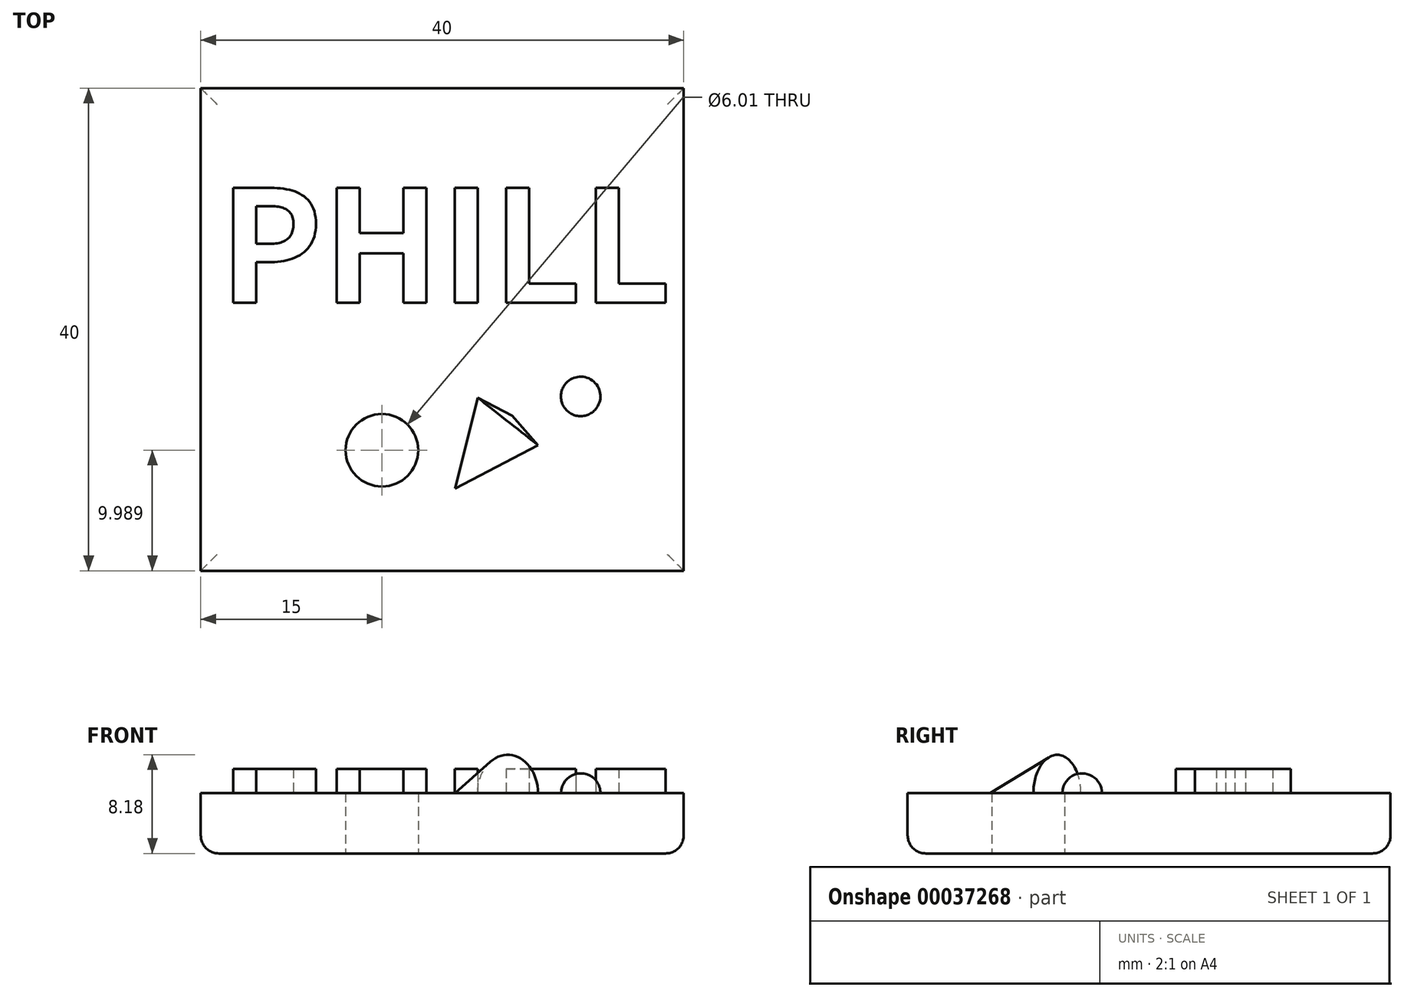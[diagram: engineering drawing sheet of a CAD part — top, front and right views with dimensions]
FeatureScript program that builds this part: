
annotation { "Feature Type Name" : "Feature", "Feature Type Description" : "" }
export const myFeature = defineFeature(function(context is Context, id is Id, definition is map)
    precondition{}
    {
        {
            var Q0;
            Q0=qCreatedBy(makeId("Top.planeOp"),FACE);
            var sketch = newSketch(context, id + "F0", { "sketchPlane" : qUnion([Q0])});
            skLineSegment(sketch, "E0", {"start": v(0, 20) * mm, "end": v(0, -20) * mm, "construction": true});
            skLineSegment(sketch, "E1.0", {"start": v(-20, 20) * mm, "end": v(-20, -20) * mm, "construction": true});
            skLineSegment(sketch, "E2", {"start": v(-20, 0) * mm, "end": v(20, 0) * mm, "construction": true});
            skLineSegment(sketch, "E3.0", {"start": v(-20, -20) * mm, "end": v(20, -20) * mm, "construction": true});
            skLineSegment(sketch, "E4.0", {"start": v(-5, 20) * mm, "end": v(-5, -20) * mm, "construction": true});
            skLineSegment(sketch, "E5.0", {"start": v(20, 20) * mm, "end": v(20, -20) * mm, "construction": true});
            skLineSegment(sketch, "E6.0", {"start": v(-20, 20) * mm, "end": v(20, 20) * mm, "construction": true});
            skPoint(sketch, "E7.orphan", {"position": v(0, 46.15) * mm});
            skPoint(sketch, "E8.orphan", {"position": v(-29, 0) * mm});
            skLineSegment(sketch, "E9", {"start": v(-20, 20) * mm, "end": v(20, 20) * mm});
            skLineSegment(sketch, "E10", {"start": v(20, -20) * mm, "end": v(20, 20) * mm});
            skLineSegment(sketch, "E11", {"start": v(-20, -20) * mm, "end": v(20, -20) * mm});
            skLineSegment(sketch, "E12", {"start": v(-20, 20) * mm, "end": v(-20, -20) * mm});
            skCircle(sketch, "E13", {"center": v(-5, -10.01) * mm, "radius": 3 * mm});
            skSolve(sketch);
        }
        {
            var Q0;
            Q0=makeQuery(id+"F0.imprint","IMPRINT",FACE,{"disambiguationData":[TD([[makeQuery(id+"F0.imprint","IMPRINT",EDGE,{"derivedFrom":sQuery(id+"F0.wireOp",EDGE,"E9")}),-1.0]])]});
            extrude(context, id + "F1", {"entities" : qUnion([Q0]), "depth" : 5 * mm});
        }
        {
            var Q0;
            Q0=makeQuery(id+"F1.opExtrude","CAP_EDGE",EDGE,{"disambiguationData":[OSD([sQuery(id+"F0.wireOp",EDGE,"E12")])],"isStart":true});
            var Q1;
            Q1=makeQuery(id+"F1.opExtrude","CAP_EDGE",EDGE,{"disambiguationData":[OSD([sQuery(id+"F0.wireOp",EDGE,"E9")])],"isStart":true});
            var Q2;
            Q2=makeQuery(id+"F1.opExtrude","CAP_EDGE",EDGE,{"disambiguationData":[OSD([sQuery(id+"F0.wireOp",EDGE,"E11")])],"isStart":true});
            var Q3;
            Q3=makeQuery(id+"F1.opExtrude","CAP_EDGE",EDGE,{"disambiguationData":[OSD([sQuery(id+"F0.wireOp",EDGE,"E10")])],"isStart":true});
            fillet(context, id + "F2", {"entities" : qUnion([Q0, Q1, Q2, Q3]), "radius" : 1.5 * mm, "tangentPropagation" : true, "allowEdgeOverflow" : false});
        }
        {
            var Q0;
            Q0=makeQuery(id+"F1.opExtrude","CAP_FACE",FACE,{"disambiguationData":[OSD([sQuery(id+"F0.wireOp",EDGE,"E9"),sQuery(id+"F0.wireOp",EDGE,"E10"),sQuery(id+"F0.wireOp",EDGE,"E11"),sQuery(id+"F0.wireOp",EDGE,"E12")])],"isStart":false});
            var sketch = newSketch(context, id + "F3", { "sketchPlane" : qUnion([Q0])});
            skLineSegment(sketch, "E14.0.0", {"start": v(-18.5, 18.5) * mm, "end": v(-18.5, -18.5) * mm});
            skLineSegment(sketch, "E14.0.1", {"start": v(-18.5, -18.5) * mm, "end": v(18.5, -18.5) * mm});
            skLineSegment(sketch, "E14.0.2", {"start": v(18.5, -18.5) * mm, "end": v(18.5, 18.5) * mm});
            skLineSegment(sketch, "E14.0.3", {"start": v(18.5, 18.5) * mm, "end": v(-18.5, 18.5) * mm});
            skText(sketch, "E15", { "text": "PHILL", "fontName": "NotoSansCJKsc-Bold.otf"});
            skCircle(sketch, "E16", {"center": v(9.55, -9.57) * mm, "radius": 4.46 * mm});
            skLineSegment(sketch, "E17", {"start": v(12.79, -6.5) * mm, "end": v(9.55, -9.57) * mm});
            skLineSegment(sketch, "E18", {"start": v(9.55, -9.57) * mm, "end": v(6.3, -12.63) * mm});
            skCircle(sketch, "E19", {"center": v(11.47, -5.54) * mm, "radius": 1.63 * mm});
            skLineSegment(sketch, "E20", {"start": v(5.8, -7.15) * mm, "end": v(1.07, -13.17) * mm});
            skLineSegment(sketch, "E21", {"start": v(1.07, -13.17) * mm, "end": v(2.93, -5.66) * mm});
            skLineSegment(sketch, "E22", {"start": v(2.93, -5.66) * mm, "end": v(5.8, -7.15) * mm});
            skLineSegment(sketch, "E23", {"start": v(12.79, -6.5) * mm, "end": v(6.3, -12.63) * mm});
            skLineSegment(sketch, "E24", {"start": v(12.79, -6.5) * mm, "end": v(10.14, -4.6) * mm});
            const initialGuessF3  = {"E15": [-0.0185, 0.0022, 1, 0, 0.00928]};
            skSetInitialGuess(sketch, initialGuessF3);
            skSolve(sketch);
        }
        {
            var Q0;
            Q0=makeQuery(id+"F3.imprint","IMPRINT",FACE,{"disambiguationData":[TD([[makeQuery(id+"F3.imprint","IMPRINT",EDGE,{"derivedFrom":sQuery(id+"F3.wireOp",EDGE,"E15.sketch_text.stroke-0")}),1.0]])]});
            var Q1;
            Q1=makeQuery(id+"F3.imprint","IMPRINT",FACE,{"disambiguationData":[TD([[makeQuery(id+"F3.imprint","IMPRINT",EDGE,{"derivedFrom":sQuery(id+"F3.wireOp",EDGE,"E15.sketch_text.stroke-12")}),1.0]])]});
            var Q2;
            Q2=makeQuery(id+"F3.imprint","IMPRINT",FACE,{"disambiguationData":[TD([[makeQuery(id+"F3.imprint","IMPRINT",EDGE,{"derivedFrom":sQuery(id+"F3.wireOp",EDGE,"E15.sketch_text.stroke-24")}),1.0]])]});
            var Q3;
            Q3=makeQuery(id+"F3.imprint","IMPRINT",FACE,{"disambiguationData":[TD([[makeQuery(id+"F3.imprint","IMPRINT",EDGE,{"derivedFrom":sQuery(id+"F3.wireOp",EDGE,"E15.sketch_text.stroke-28")}),1.0]])]});
            var Q4;
            Q4=makeQuery(id+"F3.imprint","IMPRINT",FACE,{"disambiguationData":[TD([[makeQuery(id+"F3.imprint","IMPRINT",EDGE,{"derivedFrom":sQuery(id+"F3.wireOp",EDGE,"E15.sketch_text.stroke-34")}),1.0]])]});
            extrude(context, id + "F4", {"entities" : qUnion([Q0, Q1, Q2, Q3, Q4]), "operationType" : NewBodyOperationType.ADD, "depth" : 2 * mm});
        }
        {
            var Q0;
            Q0=makeQuery(id+"F3.imprint","IMPRINT",FACE,{"disambiguationData":[TD([[makeQuery(id+"F3.imprint","IMPRINT",EDGE,{"derivedFrom":sQuery(id+"F3.wireOp",EDGE,"E20")}),-1.0]])]});
            var Q1;
            Q1=sQuery(id+"F3.wireOp",EDGE,"E20");
            revolve(context, id + "F5", {"operationType" : NewBodyOperationType.ADD, "entities" : qUnion([Q0]), "axis" : qUnion([Q1]), "revolveType" : RevolveType.FULL});
        }
        {
            var Q0;
            {var subQ0=sQuery(id+"F3.wireOp",EDGE,"E24");var subQ1=sQuery(id+"F3.wireOp",EDGE,"E19");var subQ5=makeQuery(id+"F3.imprint","INTERSECT",VERTEX,{"derivedFrom":[subQ1,subQ0]});Q0=makeQuery(id+"F3.imprint","IMPRINT",FACE,{"disambiguationData":[TD([[makeQuery(id+"F3.imprint","IMPRINT",EDGE,{"disambiguationData":[TD([[subQ5,1.0]])],"derivedFrom":subQ0}),-1.0]])]});}
            var Q1;
            {var subQ0=sQuery(id+"F3.wireOp",EDGE,"E24");var subQ1=sQuery(id+"F3.wireOp",EDGE,"E16");var subQ3=makeQuery(id+"F3.imprint","INTERSECT",VERTEX,{"derivedFrom":[subQ1,subQ0]});Q1=makeQuery(id+"F3.imprint","IMPRINT",FACE,{"disambiguationData":[TD([[makeQuery(id+"F3.imprint","IMPRINT",EDGE,{"disambiguationData":[TD([[subQ3,1.0]])],"derivedFrom":subQ1}),1.0]])]});}
            var Q2;
            Q2=sQuery(id+"F3.wireOp",EDGE,"E24");
            revolve(context, id + "F6", {"operationType" : NewBodyOperationType.ADD, "entities" : qUnion([Q0, Q1]), "axis" : qUnion([Q2]), "revolveType" : RevolveType.FULL});
        }
        {
            var Q0;
            {var subQ0=sQuery(id+"F3.wireOp",EDGE,"E23");var subQ6=makeQuery(id+"F3.imprint","IMPRINT",VERTEX,{"derivedFrom":subQ0});Q0=makeQuery(id+"F3.imprint","IMPRINT",FACE,{"disambiguationData":[TD([[makeQuery(id+"F3.imprint","IMPRINT",EDGE,{"disambiguationData":[TD([[subQ6,1.0]])],"derivedFrom":subQ0}),1.0]])]});}
            var Q1;
            {var subQ0=sQuery(id+"F3.wireOp",EDGE,"E23");var subQ1=sQuery(id+"F3.wireOp",EDGE,"E19");var subQ3=makeQuery(id+"F3.imprint","INTERSECT",VERTEX,{"derivedFrom":[subQ1,subQ0]});Q1=makeQuery(id+"F3.imprint","IMPRINT",FACE,{"disambiguationData":[TD([[makeQuery(id+"F3.imprint","IMPRINT",EDGE,{"disambiguationData":[TD([[subQ3,-1.0]])],"derivedFrom":subQ1}),1.0]])]});}
            var Q2;
            Q2=sQuery(id+"F3.wireOp",EDGE,"E17");
            revolve(context, id + "F7", {"operationType" : NewBodyOperationType.ADD, "entities" : qUnion([Q0, Q1]), "axis" : qUnion([Q2]), "revolveType" : RevolveType.FULL});
        }
    });
